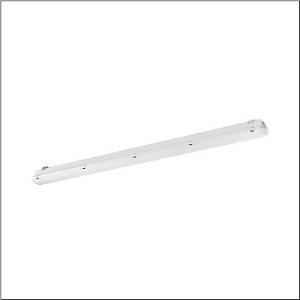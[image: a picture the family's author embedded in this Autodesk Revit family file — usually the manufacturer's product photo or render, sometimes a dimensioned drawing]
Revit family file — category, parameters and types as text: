
# Revit family: monsun_r__11xtreme_mo_51fe10dp440j_05e8
name_source: partatom
category: Lighting Fixtures
units: mm (PartAtom-declared; Revit-internal decimal feet)

## family parameters
Cut with Voids When Loaded = No
Host = Face
Light Source = No
Part Type = Normal
Room Calculation Point = No
Round Connector Dimension = Use Diameter
Shared = No

## types (1)
- --- (1 x LED, 4200 lm, 24.2 W, 4000K)
    Apparent Load = 24 VA
    CIE Flux Codes = 47 77 93 94 100
    Color Rendering = 80
    Color Temperature = 4000K
    Default Elevation = 1800 mm
    Description = Monsun® 11Xtreme MO, damp-proof luminaire, chain hanger, primary optical cover: enclosure, of PMMA, light emission: direct distribution, primary light characteristic: symmetric, installation type: suspended mounting, surface-mounted, horizontal mounting, vertical mounting, LED, rated luminous flux: 4.200lm, luminous efficacy: 174lm/W, light colour: 840, colour temperature: 4000K, control gear: ECG DALI, with terminal, 5-pole, max. 2.5mm², mains connection: 220..240V, AC, 50/60Hz, rated input power: 24W, luminaire housing, of glass-fibre reinforced polyester, uncoated, bright grey, length: 1.590mm, width: 90mm, height: 88mm, clip for enclosure, of stainless steel (V2A), ceiling mounting element, of stainless steel (V2A), chain hanger, of stainless steel (V2A), protection rating (complete): IP66, insulation class (complete): insulation class I (protective earthing), certification: CE, ENEC, VDE, UKCA, protection symbol: D, impact resistance: IK04, permissible operating ambient temperature: -25..+50°C, standard: EN 60598-2-1, EN 50419, corresponds to IFS (International Featured Standards) requirements for safety and quality in the food industry, for indoor or canopied outdoor use, no direct snow, no direct sun, no direct rain, packaging unit: 1 piece
    Height = 88 mm
    Lamp = 1 x LED
    Lamp Light Flux = 4200 lm
    Lamp Power = 24.2 W
    Lamp count = 1
    Length = 1590 mm
    Luminous efficacy = 174 lm/W
    Manufacturer = Siteco
    ModVariant = No
    Model = 51FE10DP440J
    Mounting Place = Ceiling
    Mounting Type = Pendant
    Number of Poles = 1
    OnlyDefault = Yes
    Power Factor = 1
    Product Name = Monsun® 11Xtreme MO
    Product group = damp-proof luminaire | ceiling pendant
    ProductGroupID = 908
    Protection Class = Protection class I
    Protection Degree = IP 66
    RLX_Detail_Level = 1
    RlxData = <blob elided: 87061 chars, md5=398b5e95>
    Socket = socket
    Standby Power = 0 W
    System Light Flux = 4200 lm
    System Power = 24 W
    Type Comments = factory setting: luminous flux: 100 % | dim-lin: 254 | 159 mA
    Type Image = l_1006851.jpg
    URL = http://relux.com
    VarID = @adj_121263
    Voltage = 0 V
    Weight = 0.00 kg
    Width = 90 mm

## geometry (parser evidence)
native form markers: Blend x4, Sweep x12
no freeform markers — native parametric forms only
